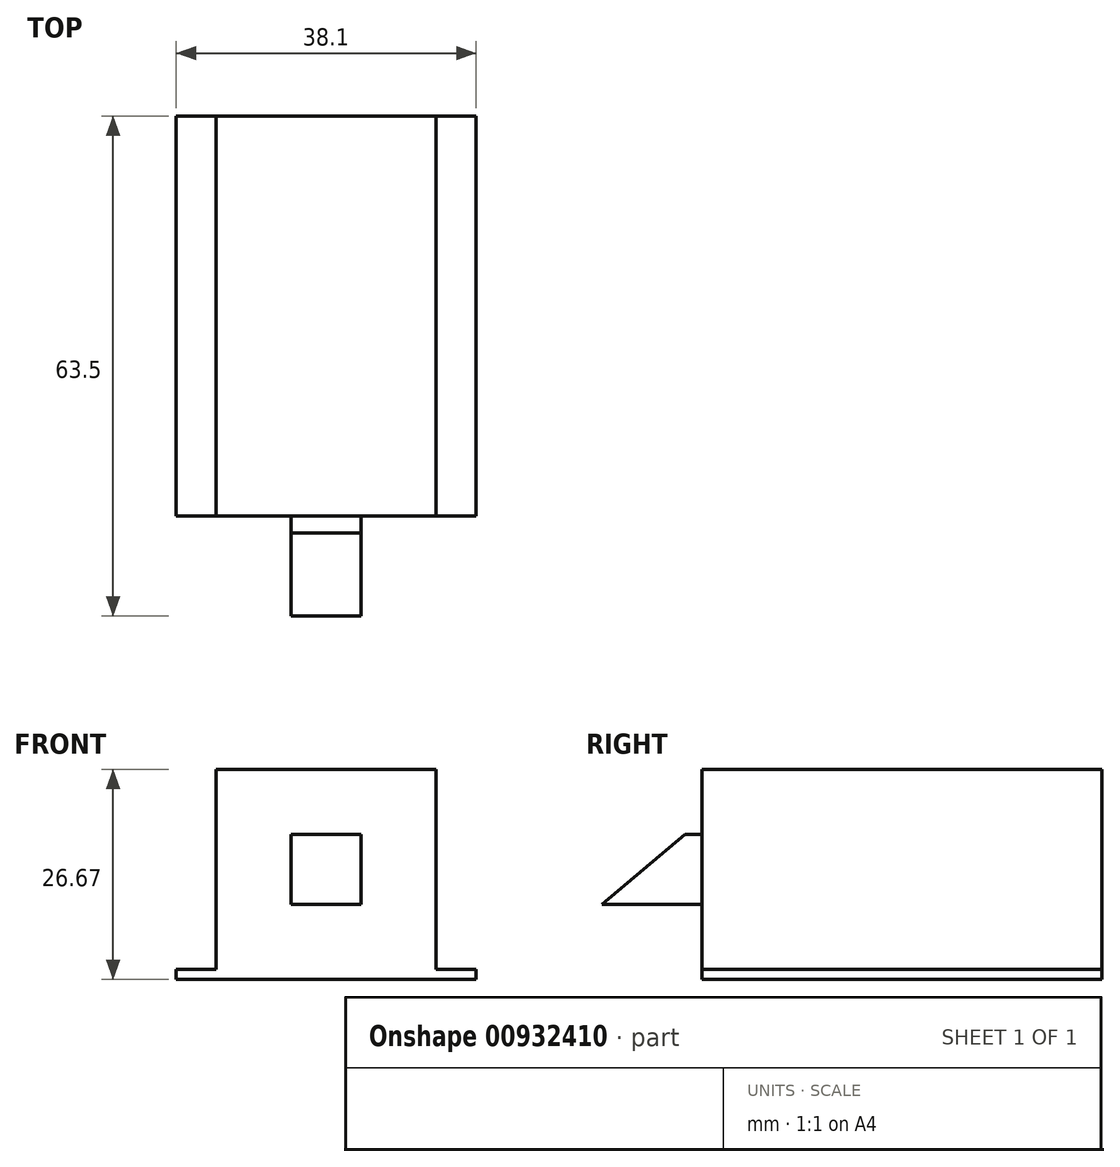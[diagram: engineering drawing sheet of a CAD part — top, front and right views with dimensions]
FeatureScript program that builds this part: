
annotation { "Feature Type Name" : "Feature", "Feature Type Description" : "" }
export const myFeature = defineFeature(function(context is Context, id is Id, definition is map)
    precondition{}
    {
        {
            var Q0;
            Q0=qCreatedBy(makeId("Top.planeOp"),FACE);
            var sketch = newSketch(context, id + "F0", { "sketchPlane" : qUnion([Q0])});
            skLineSegment(sketch, "E0.bottom", {"start": v(0, 0) * mm, "end": v(-38.1, 0) * mm});
            skLineSegment(sketch, "E0.top", {"start": v(0, 50.8) * mm, "end": v(-38.1, 50.8) * mm});
            skLineSegment(sketch, "E0.left", {"start": v(0, 0) * mm, "end": v(0, 50.8) * mm});
            skLineSegment(sketch, "E0.right", {"start": v(-38.1, 0) * mm, "end": v(-38.1, 50.8) * mm});
            skSolve(sketch);
        }
        {
            var Q0;
            Q0=makeQuery(id+"F0.imprint","IMPRINT",FACE,{"disambiguationData":[TD([[makeQuery(id+"F0.imprint","IMPRINT",EDGE,{"derivedFrom":sQuery(id+"F0.wireOp",EDGE,"E0.bottom")}),-1.0]])]});
            extrude(context, id + "F1", {"entities" : qUnion([Q0]), "depth" : 1.27 * mm, "offsetDistance" : 25.4 * mm});
        }
        {
            var Q0;
            Q0=makeQuery(id+"F1.opExtrude","CAP_FACE",FACE,{"disambiguationData":[OSD([sQuery(id+"F0.wireOp",EDGE,"E0.bottom"),sQuery(id+"F0.wireOp",EDGE,"E0.top"),sQuery(id+"F0.wireOp",EDGE,"E0.left"),sQuery(id+"F0.wireOp",EDGE,"E0.right")])],"isStart":false});
            var sketch = newSketch(context, id + "F2", { "sketchPlane" : qUnion([Q0])});
            skLineSegment(sketch, "E1", {"start": v(-33.02, 50.8) * mm, "end": v(-33.02, 0) * mm});
            skLineSegment(sketch, "E2", {"start": v(-5.08, 50.8) * mm, "end": v(-5.08, 0) * mm});
            skSolve(sketch);
        }
        {
            var Q0;
            {var subQ0=sQuery(id+"F2.wireOp",EDGE,"E1");Q0=makeQuery(id+"F2.imprint","IMPRINT",FACE,{"disambiguationData":[TD([[makeQuery(id+"F2.imprint","IMPRINT",EDGE,{"derivedFrom":subQ0}),1.0]])]});}
            extrude(context, id + "F3", {"entities" : qUnion([Q0]), "operationType" : NewBodyOperationType.ADD, "depth" : 25.4 * mm, "offsetDistance" : 25.4 * mm});
        }
        {
            var Q0;
            {var subQ0=sQuery(id+"F0.wireOp",EDGE,"E0.bottom");Q0=makeQuery(id+"F3.boolean.opBoolean","MERGE",FACE,{"derivedFrom":[makeQuery(id+"F1.opExtrude","SWEPT_FACE",FACE,{"disambiguationData":[OSD([subQ0])]}),makeQuery(id+"F3.opExtrude","SWEPT_FACE",FACE,{"disambiguationData":[OSD([subQ0])]})]});}
            var sketch = newSketch(context, id + "F4", { "sketchPlane" : qUnion([Q0])});
            skCircle(sketch, "E3", {"center": v(-19.05, 13.97) * mm, "radius": 9.53 * mm, "construction": true});
            skPoint(sketch, "E3.centerSnap0", {"position": v(-33.02, 13.97) * mm});
            skPoint(sketch, "E3.centerSnap1", {"position": v(-19.05, 26.67) * mm});
            skLineSegment(sketch, "E4.bottom", {"start": v(-23.5, 18.42) * mm, "end": v(-14.6, 18.42) * mm});
            skLineSegment(sketch, "E4.top", {"start": v(-23.5, 9.53) * mm, "end": v(-14.6, 9.53) * mm});
            skLineSegment(sketch, "E4.left", {"start": v(-23.5, 18.42) * mm, "end": v(-23.5, 9.53) * mm});
            skLineSegment(sketch, "E4.right", {"start": v(-14.6, 18.42) * mm, "end": v(-14.6, 9.53) * mm});
            skSolve(sketch);
        }
        {
            var Q0;
            Q0=makeQuery(id+"F4.imprint","IMPRINT",FACE,{"disambiguationData":[TD([[makeQuery(id+"F4.imprint","IMPRINT",EDGE,{"derivedFrom":sQuery(id+"F4.wireOp",EDGE,"E4.bottom")}),-1.0]])]});
            extrude(context, id + "F5", {"entities" : qUnion([Q0]), "operationType" : NewBodyOperationType.ADD, "depth" : 12.7 * mm, "offsetDistance" : 25.4 * mm});
        }
        {
            var Q0;
            Q0=makeQuery(id+"F5.opExtrude","SWEPT_FACE",FACE,{"disambiguationData":[OSD([sQuery(id+"F4.wireOp",EDGE,"E4.left")])]});
            var sketch = newSketch(context, id + "F6", { "sketchPlane" : qUnion([Q0])});
            skLineSegment(sketch, "E5", {"start": v(2.18, 18.42) * mm, "end": v(12.7, 9.53) * mm});
            skLineSegment(sketch, "E6", {"start": v(12.7, 9.53) * mm, "end": v(12.7, 18.42) * mm});
            skLineSegment(sketch, "E7", {"start": v(12.7, 18.42) * mm, "end": v(2.18, 18.42) * mm});
            skSolve(sketch);
        }
        {
            var Q0;
            Q0=makeQuery(id+"F6.imprint","IMPRINT",FACE,{"disambiguationData":[TD([[makeQuery(id+"F6.imprint","IMPRINT",EDGE,{"derivedFrom":sQuery(id+"F6.wireOp",EDGE,"E5")}),1.0]])]});
            extrude(context, id + "F7", {"entities" : qUnion([Q0]), "operationType" : NewBodyOperationType.REMOVE, "endBound" : BoundingType.UP_TO_NEXT, "oppositeDirection" : true, "depth" : 25.4 * mm, "offsetDistance" : 25.4 * mm});
        }
    });
